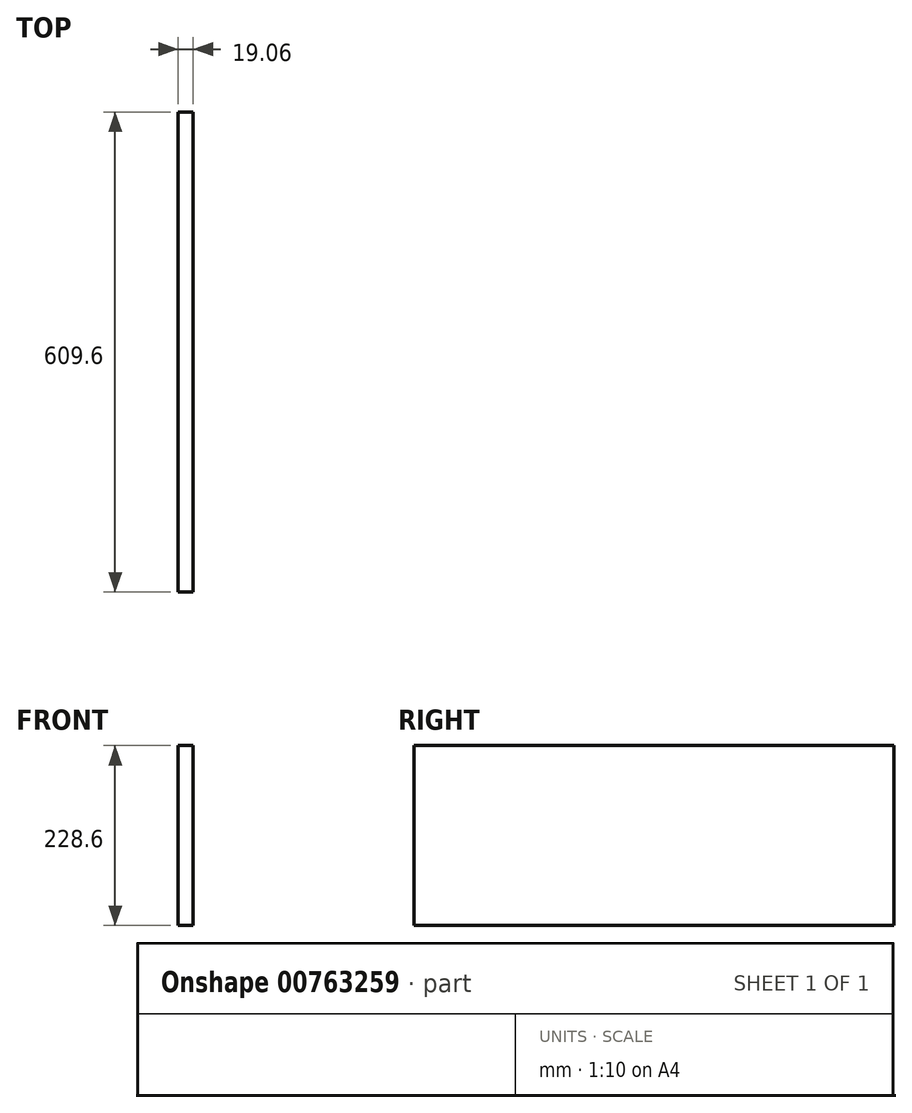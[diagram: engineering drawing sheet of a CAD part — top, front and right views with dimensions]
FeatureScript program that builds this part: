
annotation { "Feature Type Name" : "Feature", "Feature Type Description" : "" }
export const myFeature = defineFeature(function(context is Context, id is Id, definition is map)
    precondition{}
    {
        {
            var Q0;
            Q0=qCreatedBy(makeId("Top.planeOp"),FACE);
            var sketch = newSketch(context, id + "F0", { "sketchPlane" : qUnion([Q0])});
            skLineSegment(sketch, "E0.bottom", {"start": v(9.53, 304.8) * mm, "end": v(-9.52, 304.8) * mm});
            skLineSegment(sketch, "E0.top", {"start": v(9.52, -304.8) * mm, "end": v(-9.53, -304.8) * mm});
            skLineSegment(sketch, "E0.left", {"start": v(9.53, 304.8) * mm, "end": v(9.52, -304.8) * mm});
            skLineSegment(sketch, "E0.right", {"start": v(-9.52, 304.8) * mm, "end": v(-9.53, -304.8) * mm});
            skPoint(sketch, "E0.middle", {"position": v(0, 0) * mm});
            skSolve(sketch);
        }
        {
            var Q0;
            Q0 = qSketchRegion(id + "F0", true);
            extrude(context, id + "F1", {"entities" : qUnion([Q0]), "depth" : 228.6 * mm, "offsetDistance" : 25.4 * mm});
        }
    });
